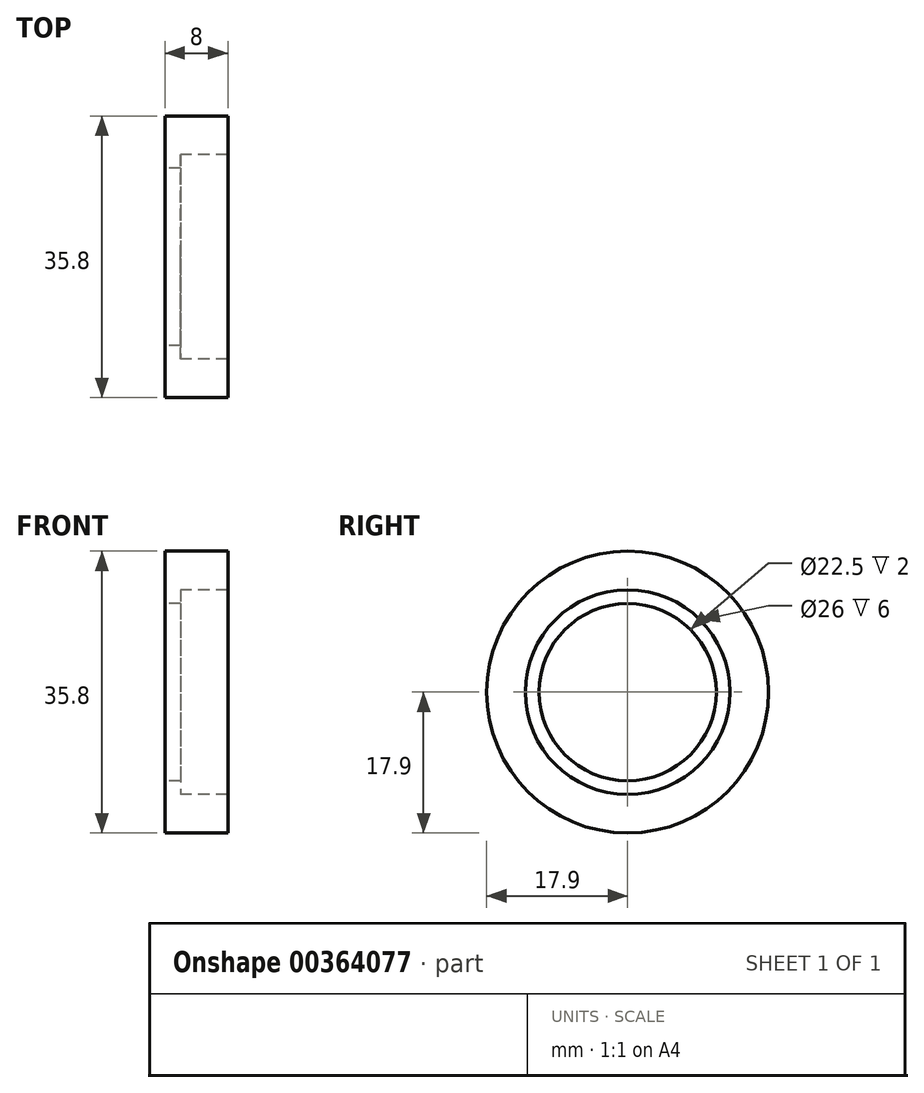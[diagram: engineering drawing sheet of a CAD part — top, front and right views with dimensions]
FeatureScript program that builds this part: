
annotation { "Feature Type Name" : "Feature", "Feature Type Description" : "" }
export const myFeature = defineFeature(function(context is Context, id is Id, definition is map)
    precondition{}
    {
        {
            var Q0;
            Q0=qCreatedBy(makeId("Right.planeOp"),FACE);
            var sketch = newSketch(context, id + "F0", { "sketchPlane" : qUnion([Q0])});
            skCircle(sketch, "E0", {"center": v(0, 0) * mm, "radius": 17.9 * mm});
            skSolve(sketch);
        }
        {
            var Q0;
            Q0 = qSketchRegion(id + "F0", true);
            extrude(context, id + "F1", {"entities" : qUnion([Q0]), "depth" : 8 * mm});
        }
        {
            var Q0;
            Q0=makeQuery(id+"F1.opExtrude","CAP_FACE",FACE,{"disambiguationData":[OSD([sQuery(id+"F0.wireOp",EDGE,"E0")])],"isStart":false});
            var sketch = newSketch(context, id + "F2", { "sketchPlane" : qUnion([Q0])});
            skPoint(sketch, "E1", {"position": v(0, 0) * mm});
            skSolve(sketch);
        }
        {
            var Q0;
            Q0=sQuery(id+"F2.wireOp",VERTEX,"E1");
            var Q1;
            Q1=makeQuery(id+"F1.opExtrude","SWEPT_BODY",BODY,{"disambiguationData":[OSD([sQuery(id+"F0.wireOp",EDGE,"E0")])]});
            hole(context, id + "F3", {"style" : HoleStyle.C_BORE, "endStyle" : HoleEndStyle.THROUGH, "holeDiameter" : 22.5 * mm, "cBoreDiameter" : 26 * mm, "cBoreDepth" : 6 * mm, "isTappedThrough" : true, "tappedDepth" : 30 * mm, "tapClearance" : 5, "locations" : qUnion([Q0]), "scope" : qUnion([Q1]), "startStyle" : HoleStartStyle.SKETCH});
        }
    });
